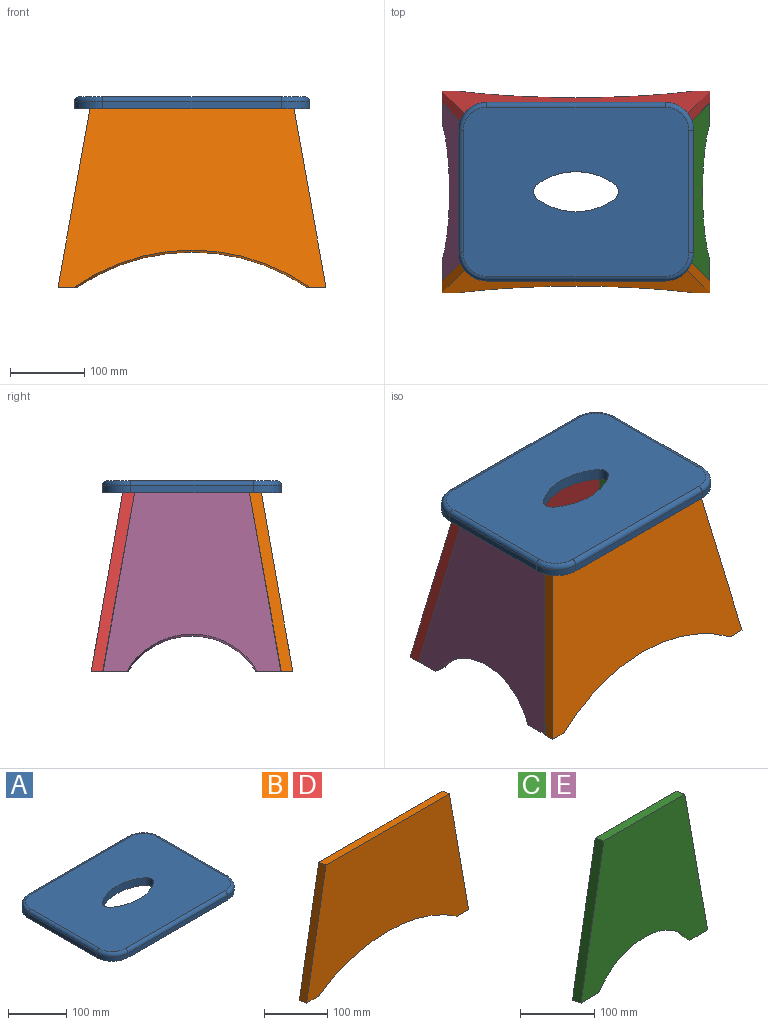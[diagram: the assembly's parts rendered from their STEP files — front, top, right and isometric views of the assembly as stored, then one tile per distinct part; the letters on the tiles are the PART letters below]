
ASSEMBLY  parts=5 mates=5
PART A: 22 faces, bbox 323.8x247.6x15.9 mm
  f0: plane 241.3x9.53mm, normal (0,1,0), area 2298.4mm2, adj f9,f10,f13,f17
  f1: plane 165.1x9.53mm, normal (-1,0,0), area 1572.6mm2, adj f9,f10,f11,f14
  f2: plane 241.3x9.53mm, normal (0,-1,0), area 2298.4mm2, adj f9,f11,f12,f18
  f3: cylinder r=12.7mm len=20.63mm, axis (0,0,-1), area 382.2mm2, adj f4,f6,f8,f9
  f4: cylinder r=88.9mm len=103.72mm, axis (0,0,-1), area 1758mm2, adj f3,f5,f8,f9
  f5: cylinder r=12.7mm len=20.63mm, axis (0,0,-1), area 382.2mm2, adj f4,f6,f8,f9
  f6: cylinder r=88.9mm len=103.72mm, axis (0,0,-1), area 1758mm2, adj f3,f5,f8,f9
  f7: plane 165.1x9.53mm, normal (1,0,0), area 1572.6mm2, adj f9,f12,f13,f21
  f8: plane 304.8x228.6mm, normal (0,0,1), area 64163.7mm2, adj f3,f4,f5,f6,f14,f15,f16,f17
  f9: plane 317.5x241.3mm, normal (0,0,-1), area 70718.4mm2, adj f0,f1,f2,f3,f4,f5,f6,f7
  f10: cylinder r=38.1mm len=38.1mm, axis (0,0,1), area 570mm2, adj f0,f1,f9,f15
  f11: cylinder r=38.1mm len=38.1mm, axis (0,0,-1), area 570mm2, adj f1,f2,f9,f16
  f12: cylinder r=38.1mm len=38.1mm, axis (0,0,1), area 570mm2, adj f2,f7,f9,f20
  f13: cylinder r=38.1mm len=38.1mm, axis (0,0,-1), area 570mm2, adj f0,f7,f9,f19
  f14: cylinder r=6.35mm len=165.1mm, axis (0,1,0), area 1646.8mm2, adj f1,f8,f15,f16
  f15: torus R=31.75mm, axis (0,0,1), area 560.8mm2, adj f8,f10,f14,f17
  f16: torus R=31.75mm, axis (0,0,1), area 560.8mm2, adj f8,f11,f14,f18
  f17: cylinder r=6.35mm len=241.3mm, axis (1,0,0), area 2406.9mm2, adj f0,f8,f15,f19
  f18: cylinder r=6.35mm len=241.3mm, axis (-1,0,0), area 2406.9mm2, adj f2,f8,f16,f20
  f19: torus R=31.75mm, axis (0,0,1), area 560.8mm2, adj f8,f13,f17,f21
  f20: torus R=31.75mm, axis (0,0,1), area 560.8mm2, adj f8,f12,f18,f21
  f21: cylinder r=6.35mm len=165.1mm, axis (0,-1,0), area 1646.8mm2, adj f7,f8,f19,f20
PART B: 8 faces, bbox 362x15.9x247.7 mm
  f0: plane 360.96x244.85mm, normal (0,-1,0), area 67726.5mm2, adj f2,f3,f4,f5,f6,f7
  f1: plane 361.95x244.85mm, normal (0,1,0), area 67091.3mm2, adj f2,f3,f4,f5,f6,f7
  f2: plane 26.35x15.88mm, normal (0,-0.17,-0.98), area 388.3mm2, adj f0,f1,f5,f7
  f3: plane 26.35x15.88mm, normal (0,-0.17,-0.98), area 388.3mm2, adj f0,f1,f4,f7
  f4: plane 247.65x43.67mm, normal (-0.98,0,0.17), area 3947mm2, adj f0,f1,f3,f6
  f5: plane 247.65x43.67mm, normal (0.98,0,0.17), area 3947mm2, adj f0,f1,f2,f6
  f6: plane 275.6x15.88mm, normal (0,0.17,0.98), area 4434.7mm2, adj f0,f1,f4,f5
  f7: cylinder r=273.05mm len=317.25mm, axis (0,1,0), area 5296.7mm2, adj f0,f1,f2,f3
PART C: 8 faces, bbox 241.3x15.9x247.7 mm
  f0: plane 244.85x240.31mm, normal (0,-1,0), area 42417.7mm2, adj f2,f3,f4,f5,f6,f7
  f1: plane 244.85x241.3mm, normal (0,1,0), area 42171.4mm2, adj f2,f3,f4,f5,f6,f7
  f2: plane 34.34x15.88mm, normal (0,-0.17,-0.98), area 535.9mm2, adj f0,f1,f5,f7
  f3: plane 34.34x15.88mm, normal (0,-0.17,-0.98), area 535.9mm2, adj f0,f1,f4,f7
  f4: plane 247.65x43.67mm, normal (-0.98,0,0.17), area 3947mm2, adj f0,f1,f3,f6
  f5: plane 247.65x43.67mm, normal (0.98,0,0.17), area 3947mm2, adj f0,f1,f2,f6
  f6: plane 154.95x15.88mm, normal (0,0.17,0.98), area 2489.9mm2, adj f0,f1,f4,f5
  f7: cylinder r=101.6mm len=175.98mm, axis (0,1,0), area 3326.4mm2, adj f0,f1,f2,f3
PART D: same geometry as B
PART E: same geometry as C
PLACE A at identity fixed
PLACE B rot(axis=(0,0.09,1),180deg) t=(0,-114.62,-119.19)mm
PLACE C rot(axis=(0.09,-0.09,-0.99),90.4deg) t=(158.32,-0.01,-119.19)mm
PLACE D rot(axis=(1,0,0),10deg) t=(0,114.61,-119.19)mm
PLACE E rot(axis=(0.09,0.09,0.99),90.4deg) t=(-158.32,-0.01,-119.19)mm
MATE parallel B.f6 <-> A.f9  axis (0,0,1) through (0,-85.55,0)mm
MATE fastened E.f6 <-> D.f6  axis (0,0,1) through (-137.31,77.47,0)mm
MATE fastened C.f6 <-> D.f6  axis (0,0,1) through (137.31,77.47,0)mm
MATE fastened E.f6 <-> B.f6  axis (0,0,1) through (-137.31,-77.48,0)mm
MATE fastened A.f9 <-> D.f6  axis (0,0,-1) through (0,0,0)mm
